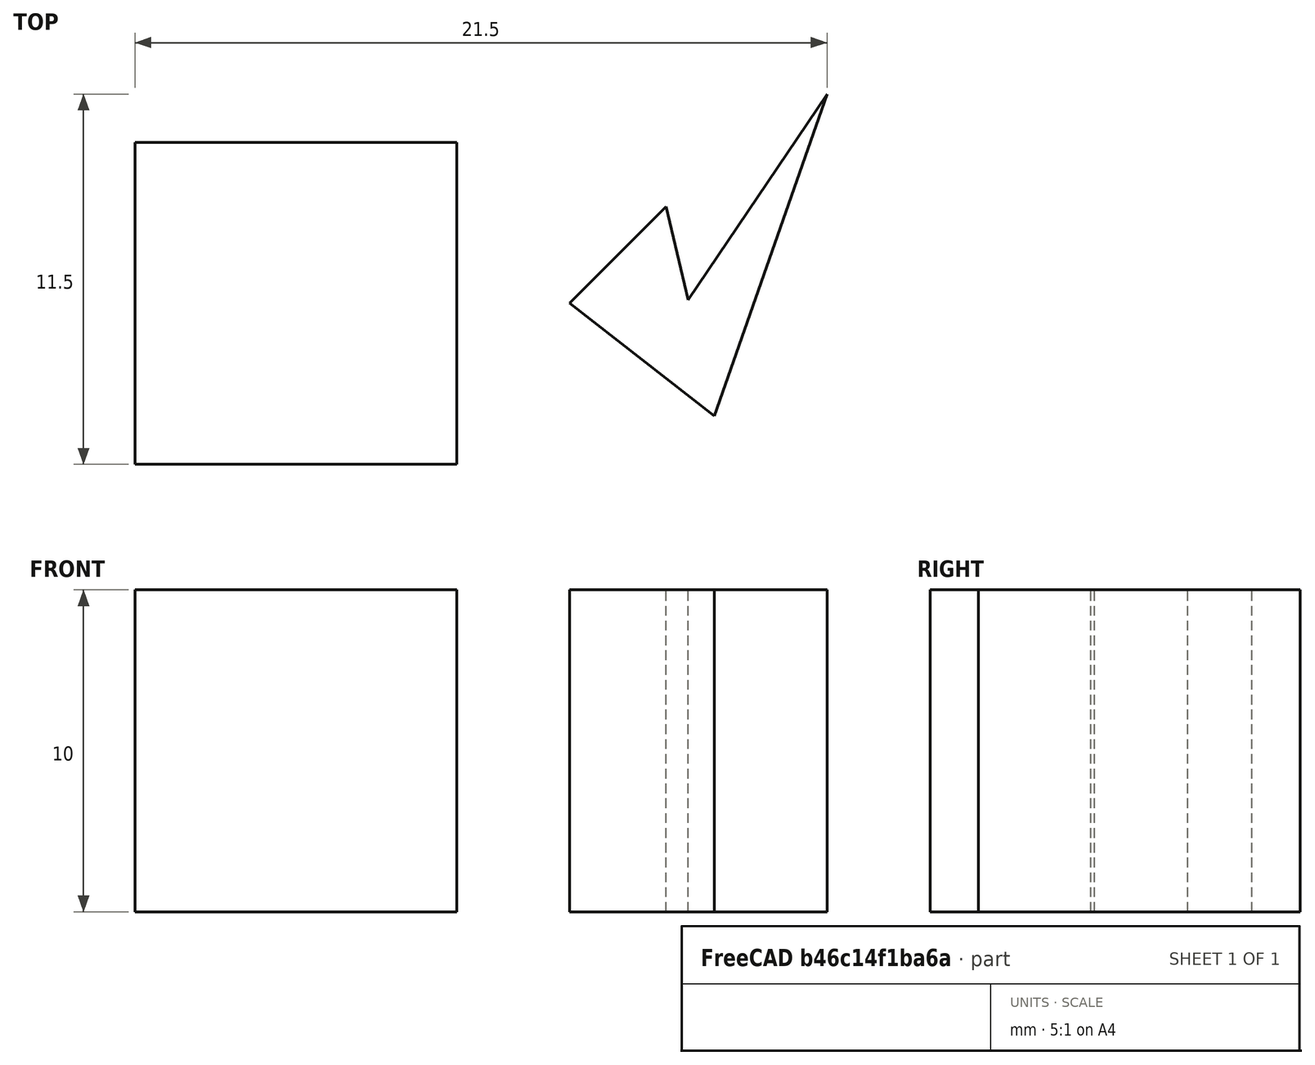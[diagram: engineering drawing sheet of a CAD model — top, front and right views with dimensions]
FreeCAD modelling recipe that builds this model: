
FCSTD DOCUMENT  (FreeCAD 0.18.4R)
Label: mink-example
License: All rights reserved
LicenseURL: http://en.wikipedia.org/wiki/All_rights_reserved
objects: Part::Box×1, Part::Part2DObjectPython×1, Part::Extrusion×1
note: 3 computed .brp shape members not serialized (recipe doc carries the construction recipe); baked Part::Feature solids carry a one-line shape summary decoded from their .brp

FEATURE [Part::Box] Box001  label="Cube001"
  AttacherType = Attacher::AttachEngine3D
  Height = 10
  Length = 10
  Width = 10
FEATURE [Part::Part2DObjectPython] Wire  # Draft 2D object (typed FeaturePython)
  ChamferSize = 0
  Closed = true
  End = (17.1855,8.10381,0)
  FilletRadius = 0
  Length = 31.2299
  MakeFace = true
  Placement = pos=(16.5,11,0) rot=(0,0,1;0rad)
  Points = (5) [(0,0,0),(-3,-3,0),(1.5,-6.5,0),(5,3.5,0),(0.685478,-2.89619,0)]
  Start = (16.5,11,0)
  Subdivisions = 0
FEATURE [Part::Extrusion] Extrude
  Base = -> Wire
  Dir = (0,0,1)
  DirMode = 2
  FaceMakerClass = Part::FaceMakerBullseye
  LengthFwd = 10
  LengthRev = 0
  Placement = pos=(0,-3,0) rot=(0,0,1;0rad)
  Solid = false
  Symmetric = false
